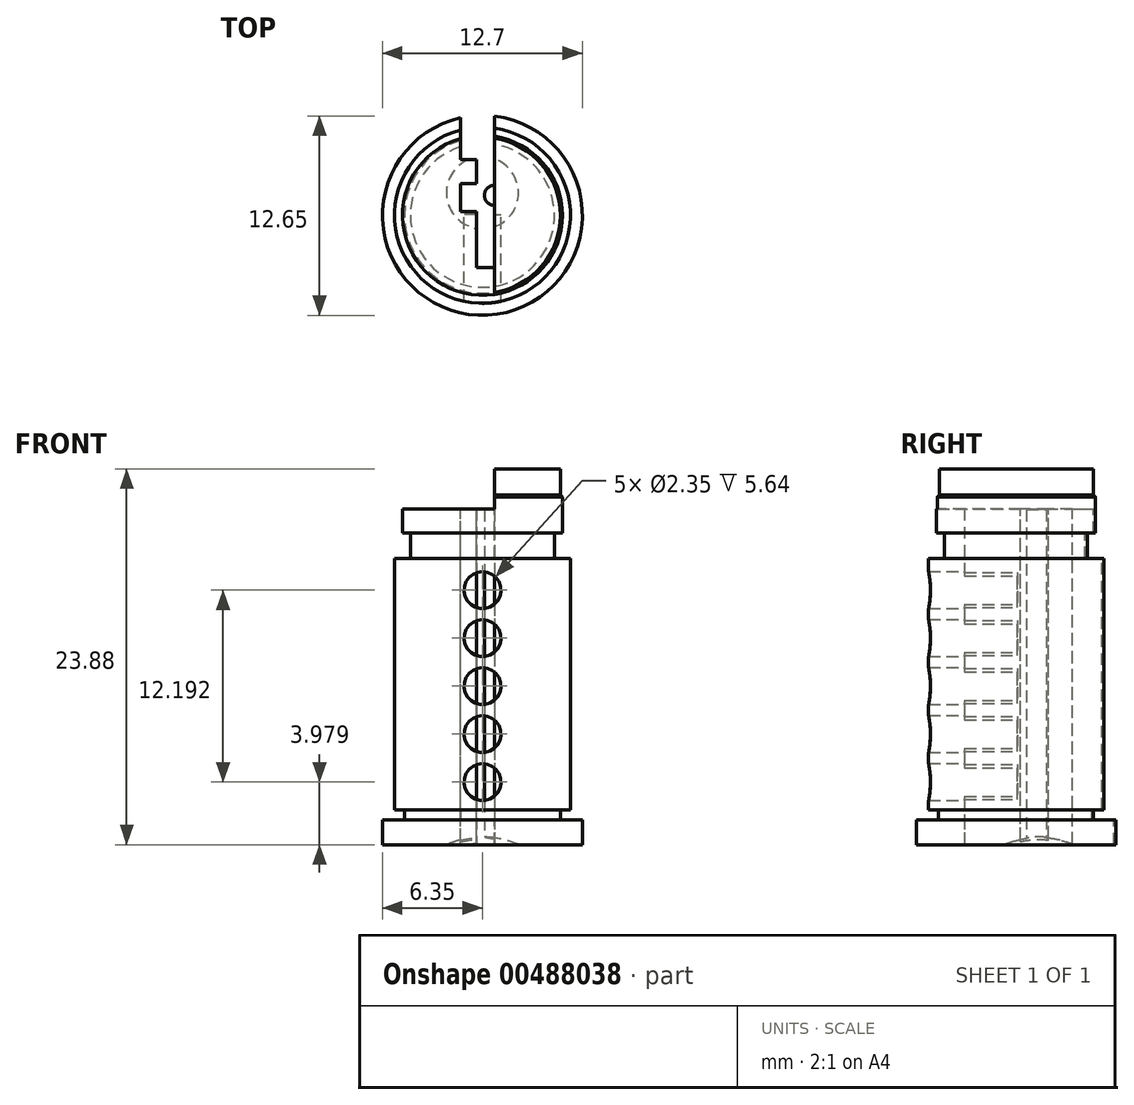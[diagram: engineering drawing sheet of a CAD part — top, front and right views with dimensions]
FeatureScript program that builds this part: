
annotation { "Feature Type Name" : "Feature", "Feature Type Description" : "" }
export const myFeature = defineFeature(function(context is Context, id is Id, definition is map)
    precondition{}
    {
        {
            var Q0;
            Q0=qCreatedBy(makeId("Top.planeOp"),FACE);
            var sketch = newSketch(context, id + "F0", { "sketchPlane" : qUnion([Q0])});
            skCircle(sketch, "E0", {"center": v(0, 0) * mm, "radius": 6.35 * mm});
            skSolve(sketch);
        }
        {
            var Q0;
            Q0 = qSketchRegion(id + "F0", true);
            extrude(context, id + "F1", {"entities" : qUnion([Q0]), "oppositeDirection" : true, "depth" : 23.88 * mm, "offsetDistance" : 25.4 * mm});
        }
        {
            var Q0;
            Q0=qCreatedBy(makeId("Top.planeOp"),FACE);
            var sketch = newSketch(context, id + "F2", { "sketchPlane" : qUnion([Q0])});
            skCircle(sketch, "E1", {"center": v(0, 0) * mm, "radius": 5.59 * mm});
            skCircle(sketch, "E2", {"center": v(0, 0) * mm, "radius": 6.35 * mm});
            skSolve(sketch);
        }
        {
            var Q0;
            Q0=makeQuery(id+"F2.imprint","IMPRINT",FACE,{"disambiguationData":[TD([[makeQuery(id+"F2.imprint","IMPRINT",EDGE,{"derivedFrom":sQuery(id+"F2.wireOp",EDGE,"E1")}),-1.0]])]});
            extrude(context, id + "F3", {"entities" : qUnion([Q0]), "operationType" : NewBodyOperationType.REMOVE, "oppositeDirection" : true, "depth" : 22.3 * mm, "offsetDistance" : 25.4 * mm});
        }
        {
            var Q0;
            Q0=makeQuery(id+"F3.boolean.opBoolean","COPY",FACE,{"derivedFrom":makeQuery(id+"F3.opExtrude","CAP_FACE",FACE,{"disambiguationData":[OSD([sQuery(id+"F2.wireOp",EDGE,"E1"),sQuery(id+"F2.wireOp",EDGE,"E2")])],"isStart":false})});
            var sketch = newSketch(context, id + "F4", { "sketchPlane" : qUnion([Q0])});
            skCircle(sketch, "E3", {"center": v(0, 0) * mm, "radius": 4.95 * mm});
            skCircle(sketch, "E4", {"center": v(0, 0) * mm, "radius": 5.84 * mm});
            skSolve(sketch);
        }
        {
            var Q0;
            Q0 = qSketchRegion(id + "F4", true);
            extrude(context, id + "F5", {"entities" : qUnion([Q0]), "operationType" : NewBodyOperationType.REMOVE, "depth" : 0.64 * mm, "offsetDistance" : 25.4 * mm});
        }
        {
            var Q0;
            Q0=qCreatedBy(makeId("Front.planeOp"),FACE);
            var sketch = newSketch(context, id + "F6", { "sketchPlane" : qUnion([Q0])});
            skCircle(sketch, "E5", {"center": v(0, -19.9) * mm, "radius": 1.17 * mm});
            skCircle(sketch, "E6.0.1.0", {"center": v(0, -16.85) * mm, "radius": 1.17 * mm});
            skCircle(sketch, "E6.0.2.0", {"center": v(0, -13.8) * mm, "radius": 1.17 * mm});
            skCircle(sketch, "E6.0.3.0", {"center": v(0, -10.76) * mm, "radius": 1.17 * mm});
            skCircle(sketch, "E6.0.4.0", {"center": v(0, -7.7) * mm, "radius": 1.17 * mm});
            skCircle(sketch, "E6.1.1.0", {"center": v(0, -16.85) * mm, "radius": 1.17 * mm});
            skCircle(sketch, "E6.1.2.0", {"center": v(0, -13.8) * mm, "radius": 1.17 * mm});
            skCircle(sketch, "E6.1.3.0", {"center": v(0, -10.76) * mm, "radius": 1.17 * mm});
            skCircle(sketch, "E6.1.4.0", {"center": v(0, -7.7) * mm, "radius": 1.17 * mm});
            skCircle(sketch, "E6.2.1.0", {"center": v(0, -16.85) * mm, "radius": 1.17 * mm});
            skCircle(sketch, "E6.2.2.0", {"center": v(0, -13.8) * mm, "radius": 1.17 * mm});
            skCircle(sketch, "E6.2.3.0", {"center": v(0, -10.76) * mm, "radius": 1.17 * mm});
            skCircle(sketch, "E6.2.4.0", {"center": v(0, -7.7) * mm, "radius": 1.17 * mm});
            skLineSegment(sketch, "E6.direction1", {"start": v(0, -19.9) * mm, "end": v(0, -19.9) * mm});
            skSolve(sketch);
        }
        {
            var Q0;
            Q0 = qSketchRegion(id + "F6", true);
            extrude(context, id + "F7", {"entities" : qUnion([Q0]), "operationType" : NewBodyOperationType.REMOVE, "depth" : 5.74 * mm, "offsetDistance" : 25.4 * mm, "hasSecondDirection" : true, "secondDirectionOppositeDirection" : true, "secondDirectionDepth" : 0.05 * mm});
        }
        {
            var Q0;
            Q0=makeQuery(id+"F1.opExtrude","CAP_FACE",FACE,{"disambiguationData":[OSD([sQuery(id+"F0.wireOp",EDGE,"E0")])],"isStart":true});
            var sketch = newSketch(context, id + "F8", { "sketchPlane" : qUnion([Q0])});
            skCircle(sketch, "E7", {"center": v(0, 0) * mm, "radius": 4.57 * mm});
            skCircle(sketch, "E8", {"center": v(0, 0) * mm, "radius": 5.72 * mm});
            skSolve(sketch);
        }
        {
            var Q0;
            Q0 = qSketchRegion(id + "F8", true);
            var Q1;
            Q1=sQuery(id+"F8.wireOp",EDGE,"E8");
            extrude(context, id + "F9", {"entities" : qUnion([Q0]), "operationType" : NewBodyOperationType.REMOVE, "surfaceEntities" : qUnion([Q1]), "endBound" : BoundingType.SYMMETRIC, "oppositeDirection" : true, "depth" : 11.38 * mm, "offsetDistance" : 25.4 * mm});
        }
        {
            var Q0;
            Q0=makeQuery(id+"F1.opExtrude","CAP_FACE",FACE,{"disambiguationData":[OSD([sQuery(id+"F0.wireOp",EDGE,"E0")])],"isStart":true});
            var sketch = newSketch(context, id + "F10", { "sketchPlane" : qUnion([Q0])});
            skCircle(sketch, "E9", {"center": v(0, 0) * mm, "radius": 5.08 * mm});
            skCircle(sketch, "E10", {"center": v(0, 0) * mm, "radius": 4.57 * mm});
            skSolve(sketch);
        }
        {
            var Q0;
            Q0 = qSketchRegion(id + "F10", true);
            extrude(context, id + "F11", {"entities" : qUnion([Q0]), "operationType" : NewBodyOperationType.ADD, "oppositeDirection" : true, "depth" : 4.1 * mm, "offsetDistance" : 25.4 * mm});
        }
        {
            var Q0;
            Q0=qCreatedBy(makeId("Front.planeOp"),FACE);
            var sketch = newSketch(context, id + "F12", { "sketchPlane" : qUnion([Q0])});
            skLineSegment(sketch, "E11.bottom", {"start": v(-7.04, 1.9) * mm, "end": v(0.76, 1.9) * mm});
            skLineSegment(sketch, "E11.top", {"start": v(-7.04, -2.54) * mm, "end": v(0.76, -2.54) * mm});
            skLineSegment(sketch, "E11.left", {"start": v(-7.04, 1.9) * mm, "end": v(-7.04, -2.54) * mm});
            skLineSegment(sketch, "E11.right", {"start": v(0.76, 1.9) * mm, "end": v(0.76, -2.54) * mm});
            skSolve(sketch);
        }
        {
            var Q0;
            Q0 = qSketchRegion(id + "F12", true);
            extrude(context, id + "F13", {"entities" : qUnion([Q0]), "operationType" : NewBodyOperationType.REMOVE, "endBound" : BoundingType.SYMMETRIC, "oppositeDirection" : true, "depth" : 11.38 * mm, "offsetDistance" : 25.4 * mm});
        }
        {
            var Q0;
            Q0=makeQuery(id+"F11.boolean.opBoolean","MERGE",FACE,{"derivedFrom":[makeQuery(id+"F1.opExtrude","CAP_FACE",FACE,{"disambiguationData":[OSD([sQuery(id+"F0.wireOp",EDGE,"E0")])],"isStart":true}),makeQuery(id+"F11.opExtrude","CAP_FACE",FACE,{"disambiguationData":[OSD([sQuery(id+"F10.wireOp",EDGE,"E9"),sQuery(id+"F10.wireOp",EDGE,"E10")])],"isStart":true})]});
            var sketch = newSketch(context, id + "F14", { "sketchPlane" : qUnion([Q0])});
            skCircle(sketch, "E12", {"center": v(0, 0) * mm, "radius": 4.95 * mm});
            skCircle(sketch, "E13", {"center": v(0, 0) * mm, "radius": 5.08 * mm});
            skSolve(sketch);
        }
        {
            var Q0;
            Q0 = qSketchRegion(id + "F14", true);
            extrude(context, id + "F15", {"entities" : qUnion([Q0]), "operationType" : NewBodyOperationType.REMOVE, "oppositeDirection" : true, "depth" : 1.78 * mm, "offsetDistance" : 25.4 * mm});
        }
        {
            var Q0;
            Q0=makeQuery(id+"F15.boolean.opBoolean","COPY",EDGE,{"derivedFrom":makeQuery(id+"F15.opExtrude","CAP_EDGE",EDGE,{"disambiguationData":[OSD([sQuery(id+"F14.wireOp",EDGE,"E12")])],"isStart":false})});
            chamfer(context, id + "F16", {"entities" : qUnion([Q0]), "width" : 0.13 * mm, "tangentPropagation" : true});
        }
        {
            var Q0;
            Q0=makeQuery(id+"F1.opExtrude","CAP_FACE",FACE,{"disambiguationData":[OSD([sQuery(id+"F0.wireOp",EDGE,"E0")])],"isStart":false});
            var sketch = newSketch(context, id + "F17", { "sketchPlane" : qUnion([Q0])});
            skLineSegment(sketch, "E14.top", {"start": v(-0.38, 3.3) * mm, "end": v(0.76, 3.3) * mm});
            skLineSegment(sketch, "E14.left", {"start": v(-0.38, -6.35) * mm, "end": v(-0.38, 3.3) * mm});
            skLineSegment(sketch, "E14.right", {"start": v(0.76, -6.35) * mm, "end": v(0.76, 3.3) * mm});
            skLineSegment(sketch, "E15", {"start": v(0.76, -6.35) * mm, "end": v(-0.38, -6.35) * mm});
            skSolve(sketch);
        }
        {
            var Q0;
            Q0 = qSketchRegion(id + "F17", true);
            extrude(context, id + "F18", {"entities" : qUnion([Q0]), "operationType" : NewBodyOperationType.REMOVE, "endBound" : BoundingType.THROUGH_ALL, "oppositeDirection" : true, "depth" : 25.4 * mm, "offsetDistance" : 25.4 * mm});
        }
        {
            var Q0;
            Q0=makeQuery(id+"F13.boolean.opBoolean","COPY",FACE,{"derivedFrom":makeQuery(id+"F13.opExtrude","SWEPT_FACE",FACE,{"disambiguationData":[OSD([sQuery(id+"F12.wireOp",EDGE,"E11.top")])]})});
            var sketch = newSketch(context, id + "F19", { "sketchPlane" : qUnion([Q0])});
            skLineSegment(sketch, "E16.bottom", {"start": v(-0.38, 3.54) * mm, "end": v(-1.4, 3.54) * mm});
            skLineSegment(sketch, "E16.top", {"start": v(-0.38, 5.07) * mm, "end": v(-1.4, 5.07) * mm});
            skLineSegment(sketch, "E16.left", {"start": v(-0.38, 3.54) * mm, "end": v(-0.38, 5.07) * mm});
            skLineSegment(sketch, "E16.right", {"start": v(-1.4, 3.54) * mm, "end": v(-1.4, 5.07) * mm});
            skSolve(sketch);
        }
        {
            var Q0;
            Q0 = qSketchRegion(id + "F19", true);
            extrude(context, id + "F20", {"entities" : qUnion([Q0]), "operationType" : NewBodyOperationType.REMOVE, "oppositeDirection" : true, "depth" : 21.95 * mm, "offsetDistance" : 25.4 * mm});
        }
        {
            var Q0;
            Q0=makeQuery(id+"F20.boolean.opBoolean","COPY",FACE,{"derivedFrom":makeQuery(id+"F20.opExtrude","SWEPT_FACE",FACE,{"disambiguationData":[OSD([sQuery(id+"F19.wireOp",EDGE,"E16.top")])]})});
            var sketch = newSketch(context, id + "F21", { "sketchPlane" : qUnion([Q0])});
            skLineSegment(sketch, "E17.bottom", {"start": v(-1.4, -22.3) * mm, "end": v(-0.38, -22.3) * mm});
            skLineSegment(sketch, "E17.top", {"start": v(-1.4, -23.88) * mm, "end": v(-0.38, -23.88) * mm});
            skLineSegment(sketch, "E17.left", {"start": v(-1.4, -22.3) * mm, "end": v(-1.4, -23.88) * mm});
            skLineSegment(sketch, "E17.right", {"start": v(-0.38, -22.3) * mm, "end": v(-0.38, -23.88) * mm});
            skSolve(sketch);
        }
        {
            var Q0;
            Q0 = qSketchRegion(id + "F21", true);
            extrude(context, id + "F22", {"entities" : qUnion([Q0]), "operationType" : NewBodyOperationType.REMOVE, "oppositeDirection" : true, "depth" : 1.93 * mm, "offsetDistance" : 25.4 * mm});
        }
        {
            var Q0;
            Q0=makeQuery(id+"F13.boolean.opBoolean","COPY",FACE,{"derivedFrom":makeQuery(id+"F13.opExtrude","SWEPT_FACE",FACE,{"disambiguationData":[OSD([sQuery(id+"F12.wireOp",EDGE,"E11.top")])]})});
            var sketch = newSketch(context, id + "F23", { "sketchPlane" : qUnion([Q0])});
            skLineSegment(sketch, "E18.bottom", {"start": v(-1.4, 2.03) * mm, "end": v(-0.38, 2.03) * mm});
            skLineSegment(sketch, "E18.top", {"start": v(-1.4, 0.25) * mm, "end": v(-0.38, 0.25) * mm});
            skLineSegment(sketch, "E18.left", {"start": v(-1.4, 2.03) * mm, "end": v(-1.4, 0.25) * mm});
            skLineSegment(sketch, "E18.right", {"start": v(-0.38, 2.03) * mm, "end": v(-0.38, 0.25) * mm});
            skSolve(sketch);
        }
        {
            var Q0;
            Q0 = qSketchRegion(id + "F23", true);
            var Q1;
            Q1=makeQuery(id+"F1.opExtrude","CAP_FACE",FACE,{"disambiguationData":[OSD([sQuery(id+"F0.wireOp",EDGE,"E0")])],"isStart":false});
            extrude(context, id + "F24", {"entities" : qUnion([Q0]), "operationType" : NewBodyOperationType.REMOVE, "endBound" : BoundingType.UP_TO_SURFACE, "oppositeDirection" : true, "depth" : 21.7 * mm, "endBoundEntityFace" : qUnion([Q1]), "offsetDistance" : 25.4 * mm});
        }
        {
            var Q0;
            Q0=makeQuery(id+"F1.opExtrude","CAP_FACE",FACE,{"disambiguationData":[OSD([sQuery(id+"F0.wireOp",EDGE,"E0")])],"isStart":false});
            var sketch = newSketch(context, id + "F25", { "sketchPlane" : qUnion([Q0])});
            skCircle(sketch, "E19", {"center": v(0.76, -1.27) * mm, "radius": 0.64 * mm});
            skPoint(sketch, "E19.centerSnap0", {"position": v(-1.4, -1.14) * mm});
            skSolve(sketch);
        }
        {
            var Q0;
            Q0 = qSketchRegion(id + "F25", true);
            var Q1;
            Q1=makeQuery(id+"F11.boolean.opBoolean","MERGE",FACE,{"derivedFrom":[makeQuery(id+"F1.opExtrude","CAP_FACE",FACE,{"disambiguationData":[OSD([sQuery(id+"F0.wireOp",EDGE,"E0")])],"isStart":true}),makeQuery(id+"F11.opExtrude","CAP_FACE",FACE,{"disambiguationData":[OSD([sQuery(id+"F10.wireOp",EDGE,"E9"),sQuery(id+"F10.wireOp",EDGE,"E10")])],"isStart":true})]});
            var Q2;
            Q2=makeQuery(id+"F1.opExtrude","SWEPT_BODY",BODY,{"disambiguationData":[OSD([sQuery(id+"F0.wireOp",EDGE,"E0")])]});
            extrude(context, id + "F26", {"entities" : qUnion([Q0]), "operationType" : NewBodyOperationType.ADD, "oppositeDirection" : true, "depth" : 21.29 * mm, "endBoundEntityFace" : qUnion([Q1]), "endBoundEntityBody" : qUnion([Q2]), "offsetDistance" : 25.4 * mm});
        }
        {
            var Q0;
            Q0=qCreatedBy(makeId("Right.planeOp"),FACE);
            var sketch = newSketch(context, id + "F27", { "sketchPlane" : qUnion([Q0])});
            skLineSegment(sketch, "E20", {"start": v(1.43, -23.37) * mm, "end": v(1.43, -23.88) * mm});
            skLineSegment(sketch, "E21", {"start": v(1.43, -23.88) * mm, "end": v(-0.86, -23.88) * mm});
            skArc(sketch, "E22", {"start": v(1.43, -23.37) * mm, "mid": v(0.26, -23.52) * mm, "end": v(-0.86, -23.88) * mm});
            skSolve(sketch);
        }
        {
            var Q0;
            Q0 = qSketchRegion(id + "F27", true);
            var Q1;
            Q1=sQuery(id+"F27.wireOp",EDGE,"E20");
            revolve(context, id + "F28", {"operationType" : NewBodyOperationType.REMOVE, "entities" : qUnion([Q0]), "axis" : qUnion([Q1]), "revolveType" : RevolveType.FULL, "oppositeDirection" : true});
        }
        {
            var Q0;
            Q0=makeQuery(id+"F9.boolean.opBoolean","COPY",FACE,{"derivedFrom":makeQuery(id+"F9.opExtrude","CAP_FACE",FACE,{"disambiguationData":[OSD([sQuery(id+"F8.wireOp",EDGE,"E7"),sQuery(id+"F8.wireOp",EDGE,"E8")])],"isStart":false})});
            var sketch = newSketch(context, id + "F29", { "sketchPlane" : qUnion([Q0])});
            skLineSegment(sketch, "E23.bottom", {"start": v(-1.4, 4.84) * mm, "end": v(-0.23, 4.84) * mm});
            skLineSegment(sketch, "E23.top", {"start": v(-1.4, 5.71) * mm, "end": v(-0.23, 5.71) * mm});
            skLineSegment(sketch, "E23.left", {"start": v(-1.4, 4.84) * mm, "end": v(-1.4, 5.71) * mm});
            skLineSegment(sketch, "E23.right", {"start": v(-0.23, 4.84) * mm, "end": v(-0.23, 5.71) * mm});
            skSolve(sketch);
        }
        {
            var Q0;
            Q0 = qSketchRegion(id + "F29", true);
            extrude(context, id + "F30", {"entities" : qUnion([Q0]), "operationType" : NewBodyOperationType.REMOVE, "oppositeDirection" : true, "depth" : 25.4 * mm, "offsetDistance" : 25.4 * mm});
        }
    });
